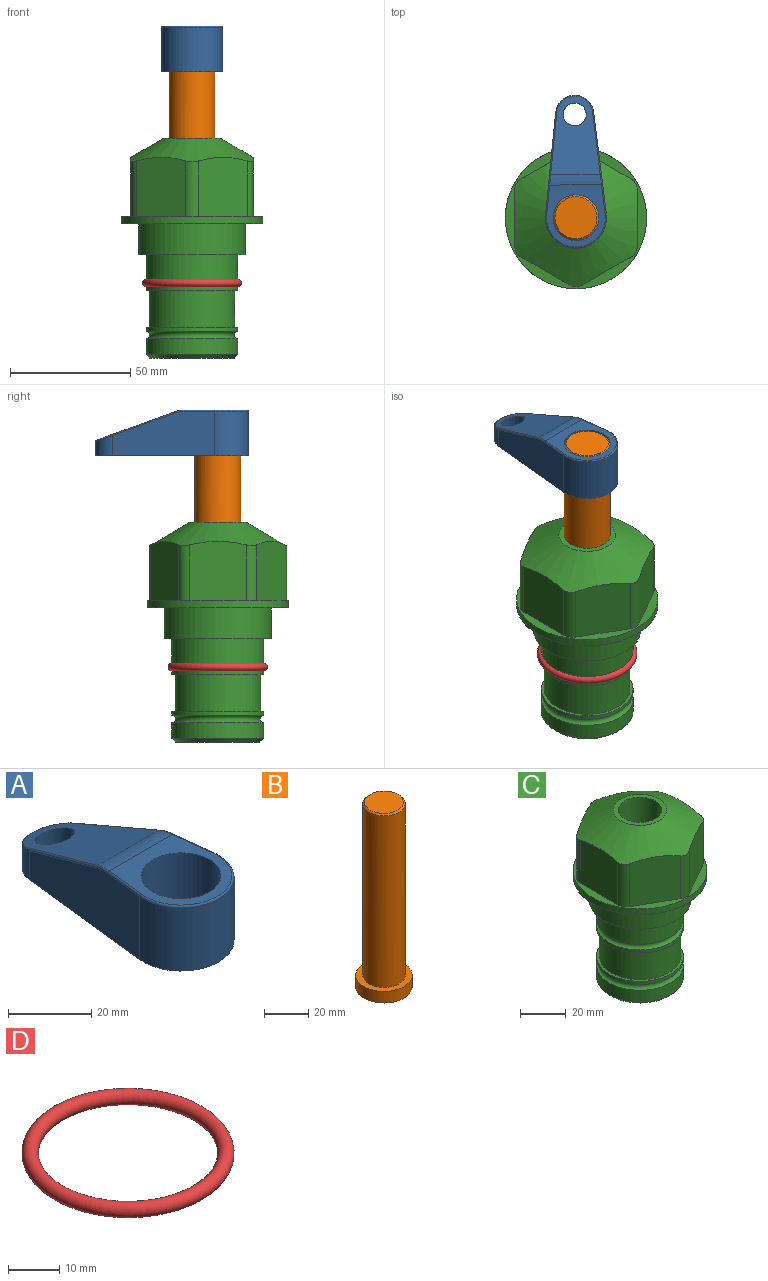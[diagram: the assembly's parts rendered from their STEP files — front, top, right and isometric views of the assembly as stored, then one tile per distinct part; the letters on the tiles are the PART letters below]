
ASSEMBLY  parts=4 mates=2
PART A: 44 faces, bbox 27.5x64.5x19.1 mm
  f0: plane 2.3x0.95mm, normal (0,0,-1), area 1mm2, adj f25,f30,f34
  f1: plane 63.5x25.4mm, normal (0,0,-1), area 561.7mm2, adj f2,f3,f4,f5,f6,f7,f19,f20
  f2: cylinder r=12.7mm len=25.4mm, axis (0,0,-1), area 792.2mm2, adj f1,f3,f5,f13
  f3: plane 42.33x18.54mm, normal (0.99,0.11,0), area 647mm2, adj f1,f2,f4,f11,f12,f14
  f4: cylinder r=7.94mm len=15.78mm, axis (0,0,-1), area 158.6mm2, adj f1,f3,f5,f16
  f5: plane 42.33x18.54mm, normal (-0.99,0.11,0), area 647mm2, adj f1,f2,f4,f15,f17,f18
  f6: cylinder r=9.53mm len=19.05mm, axis (0,0,-1), area 1140.1mm2, adj f1,f8
  f7: cylinder r=4.76mm len=10.98mm, axis (0,0,-1), area 276.1mm2, adj f1,f9
  f8: plane 25.83x24.38mm, normal (0,0,1), area 262.2mm2, adj f6,f10,f11,f13,f15
  f9: plane 32.49x20.55mm, normal (0,0.34,0.94), area 489.9mm2, adj f7,f10,f14,f16,f18
  f10: cylinder r=12.7mm len=21.49mm, axis (-1,0,0), area 93.2mm2, adj f8,f9,f12,f17
  f11: cylinder r=0.51mm len=12.34mm, axis (0.11,-0.99,0), area 9.9mm2, adj f3,f8,f12,f13
  f12: bspline ~7.62x1.64mm, area 3.5mm2, adj f3,f10,f11,f14
  f13: torus R=12.19mm, axis (0,0,1), area 33.6mm2, adj f2,f8,f11,f15
  f14: cylinder r=0.51mm len=26.01mm, axis (0.1,-0.93,0.34), area 21.6mm2, adj f3,f9,f12,f16
  f15: cylinder r=0.51mm len=12.34mm, axis (0.11,0.99,0), area 9.9mm2, adj f5,f8,f13,f17
  f16: bspline ~15.78x7.05mm, area 15.7mm2, adj f4,f9,f14,f18
  f17: bspline ~7.62x1.64mm, area 3.5mm2, adj f5,f10,f15,f18
  f18: cylinder r=0.51mm len=26.01mm, axis (0.1,0.93,-0.34), area 21.6mm2, adj f5,f9,f16,f17
  f19: plane 21.6x14.29mm, normal (-0.99,-0.11,0), area 242.6mm2, adj f1,f26,f28,f34,f36,f38
  f20: plane 21.6x14.29mm, normal (0.99,-0.11,0), area 242.6mm2, adj f1,f27,f29,f37,f39,f41
  f21: cylinder r=12.7mm len=14.29mm, axis (0,0,-1), area 173.2mm2, adj f1,f26,f27,f30,f31,f33
  f22: cylinder r=7.94mm len=7.63mm, axis (0,0,-1), area 53.8mm2, adj f1,f28,f29,f42
  f23: plane 2.3x0.95mm, normal (0,0,-1), area 1mm2, adj f25,f33,f37
  f24: plane 17.94x12.32mm, normal (0,-0.34,-0.94), area 191.2mm2, adj f25,f38,f41,f42
  f25: cylinder r=9.53mm len=12.93mm, axis (-1,0,0), area 37.5mm2, adj f0,f23,f24,f31,f36,f39
  f26: cylinder r=1.59mm len=14.29mm, axis (0,0,-1), area 49mm2, adj f1,f19,f21,f32
  f27: cylinder r=1.59mm len=14.29mm, axis (0,0,-1), area 49mm2, adj f1,f20,f21,f35
  f28: cylinder r=1.59mm len=7.28mm, axis (0,0,-1), area 22.1mm2, adj f1,f19,f22,f40
  f29: cylinder r=1.59mm len=7.28mm, axis (0,0,-1), area 22.1mm2, adj f1,f20,f22,f43
  f30: torus R=14.29mm, axis (0,0,1), area 5.8mm2, adj f0,f21,f31,f32
  f31: bspline ~11.06x2.73mm, area 20.8mm2, adj f21,f25,f30,f33
  f32: sphere r=1.59mm, area 5.4mm2, adj f26,f30,f34
  f33: torus R=14.29mm, axis (0,0,1), area 5.8mm2, adj f21,f23,f31,f35
  f34: cylinder r=1.59mm len=1.68mm, axis (-0.11,0.99,0), area 2.4mm2, adj f0,f19,f32,f36
  f35: sphere r=1.59mm, area 5.4mm2, adj f27,f33,f37
  f36: bspline ~5.82x2.33mm, area 7.7mm2, adj f19,f25,f34,f38
  f37: cylinder r=1.59mm len=1.68mm, axis (0.11,0.99,0), area 2.4mm2, adj f20,f23,f35,f39
  f38: cylinder r=1.59mm len=18.33mm, axis (0.1,-0.93,0.34), area 46.7mm2, adj f19,f24,f36,f40
  f39: bspline ~5.82x2.33mm, area 7.7mm2, adj f20,f25,f37,f41
  f40: sphere r=1.59mm, area 3.6mm2, adj f28,f38,f42
  f41: cylinder r=1.59mm len=18.33mm, axis (0.1,0.93,-0.34), area 46.7mm2, adj f20,f24,f39,f43
  f42: bspline ~8.31x1.84mm, area 15.3mm2, adj f22,f24,f40,f43
  f43: sphere r=1.59mm, area 3.6mm2, adj f29,f41,f42
PART B: 6 faces, bbox 25.4x25.4x101.6 mm
  f0: plane 17.46x17.46mm, normal (0,0,1), area 239.5mm2, adj f5
  f1: plane 25.4x25.4mm, normal (0,0,-1), area 506.7mm2, adj f2
  f2: cylinder r=12.7mm len=25.4mm, axis (0,0,1), area 506.7mm2, adj f1,f3
  f3: plane 25.4x25.4mm, normal (0,0,1), area 221.7mm2, adj f2,f4
  f4: cylinder r=9.53mm len=94.46mm, axis (0,0,1), area 5653mm2, adj f3,f5
  f5: cone r=8.73mm half-angle=45deg, axis (0,0,-1), area 64.4mm2, adj f0,f4
PART C: 36 faces, bbox 58.7x58.7x91.2 mm
  f0: cylinder r=17.78mm len=35.56mm, axis (0,0,1), area 1670.8mm2, adj f23,f24,f31
  f1: cylinder r=19.05mm len=38.1mm, axis (0,0,1), area 1191.9mm2, adj f26,f27,f30
  f2: plane 58.66x58.66mm, normal (0,0,-1), area 1150.6mm2, adj f3,f28
  f3: cylinder r=29.33mm len=58.66mm, axis (0,0,-1), area 585.1mm2, adj f2,f4
  f4: plane 58.66x58.66mm, normal (0,0,1), area 475.9mm2, adj f3,f5,f6,f7,f8,f9,f10,f11
  f5: plane 24.5x20.32mm, normal (-0.5,0.87,0), area 562.8mm2, adj f4,f15,f16,f17
  f6: plane 24.5x20.32mm, normal (0.5,0.87,0), area 562.8mm2, adj f4,f14,f15,f17
  f7: plane 24.5x23.48mm, normal (1,0,0), area 562.8mm2, adj f4,f13,f14,f17
  f8: plane 24.5x20.32mm, normal (0.5,-0.87,0), area 562.8mm2, adj f4,f12,f13,f17
  f9: plane 24.5x20.32mm, normal (-0.5,-0.87,0), area 562.8mm2, adj f4,f11,f12,f17
  f10: plane 24.5x23.48mm, normal (-1,0,0), area 562.8mm2, adj f4,f11,f16,f17
  f11: cylinder r=5.08mm len=23.01mm, axis (0,0,-1), area 121.2mm2, adj f4,f9,f10,f17
  f12: cylinder r=5.08mm len=23.01mm, axis (0,0,-1), area 121.2mm2, adj f4,f8,f9,f17
  f13: cylinder r=5.08mm len=23.01mm, axis (0,0,-1), area 121.2mm2, adj f4,f7,f8,f17
  f14: cylinder r=5.08mm len=23.01mm, axis (0,0,-1), area 121.2mm2, adj f4,f6,f7,f17
  f15: cylinder r=5.08mm len=23.01mm, axis (0,0,-1), area 121.2mm2, adj f4,f5,f6,f17
  f16: cylinder r=5.08mm len=23.01mm, axis (0,0,-1), area 121.2mm2, adj f4,f5,f10,f17
  f17: cone r=11.73mm half-angle=60deg, axis (0,0,-1), area 2071.8mm2, adj f5,f6,f7,f8,f9,f10,f11,f12
  f18: plane 23.46x23.46mm, normal (0,0,1), area 147.4mm2, adj f17,f35
  f19: plane 34.93x34.93mm, normal (0,0,-1), area 958mm2, adj f29
  f20: cylinder r=19.05mm len=38.1mm, axis (0,0,1), area 760.1mm2, adj f21,f29
  f21: torus R=19.05mm, axis (0,0,1), area 565.3mm2, adj f20,f22
  f22: cylinder r=19.05mm len=38.1mm, axis (0,0,1), area 190mm2, adj f21,f23
  f23: plane 38.1x38.1mm, normal (0,0,1), area 146.9mm2, adj f0,f22
  f24: plane 38.1x38.1mm, normal (0,0,-1), area 146.9mm2, adj f0,f25
  f25: cylinder r=19.05mm len=38.1mm, axis (0,0,1), area 190mm2, adj f24,f26
  f26: torus R=19.05mm, axis (0,0,1), area 565.3mm2, adj f1,f25
  f27: plane 44.45x44.45mm, normal (0,0,-1), area 411.7mm2, adj f1,f28
  f28: cylinder r=22.23mm len=44.45mm, axis (0,0,1), area 1773.5mm2, adj f2,f27
  f29: cone r=19.05mm half-angle=45deg, axis (0,0,1), area 257.5mm2, adj f19,f20
  f30: cylinder r=3.17mm len=6.75mm, axis (-1,0,0), area 128mm2, adj f1,f33
  f31: cylinder r=3.17mm len=6.35mm, axis (-1,0,0), area 102.5mm2, adj f0,f33
  f32: plane 25.4x25.4mm, normal (0,0,1), area 506.7mm2, adj f33
  f33: cylinder r=12.7mm len=66.42mm, axis (0,0,-1), area 5236.2mm2, adj f30,f31,f32,f34
  f34: cone r=9.53mm half-angle=30deg, axis (0,0,-1), area 443.4mm2, adj f33,f35
  f35: cylinder r=9.53mm len=19.05mm, axis (0,0,-1), area 849mm2, adj f18,f34
PART D: 1 faces, bbox 44.7x44.7x3.2 mm
  f0: torus R=19.05mm, axis (0,0,1), area 1193.9mm2
PLACE A rot(axis=(0,0,1),0.7deg) t=(0,0,63.12)mm
PLACE B rot(axis=(0,0,1),0.7deg) t=(0,0,8.51)mm
PLACE C at identity fixed
PLACE D at identity
MATE cylindrical B.f2 <-> C.f0  axis (0,0,1) through (0,0,34.15)mm
MATE fastened A.f2 <-> B.f2  axis (0,0,-1) through (0,0,82.17)mm
